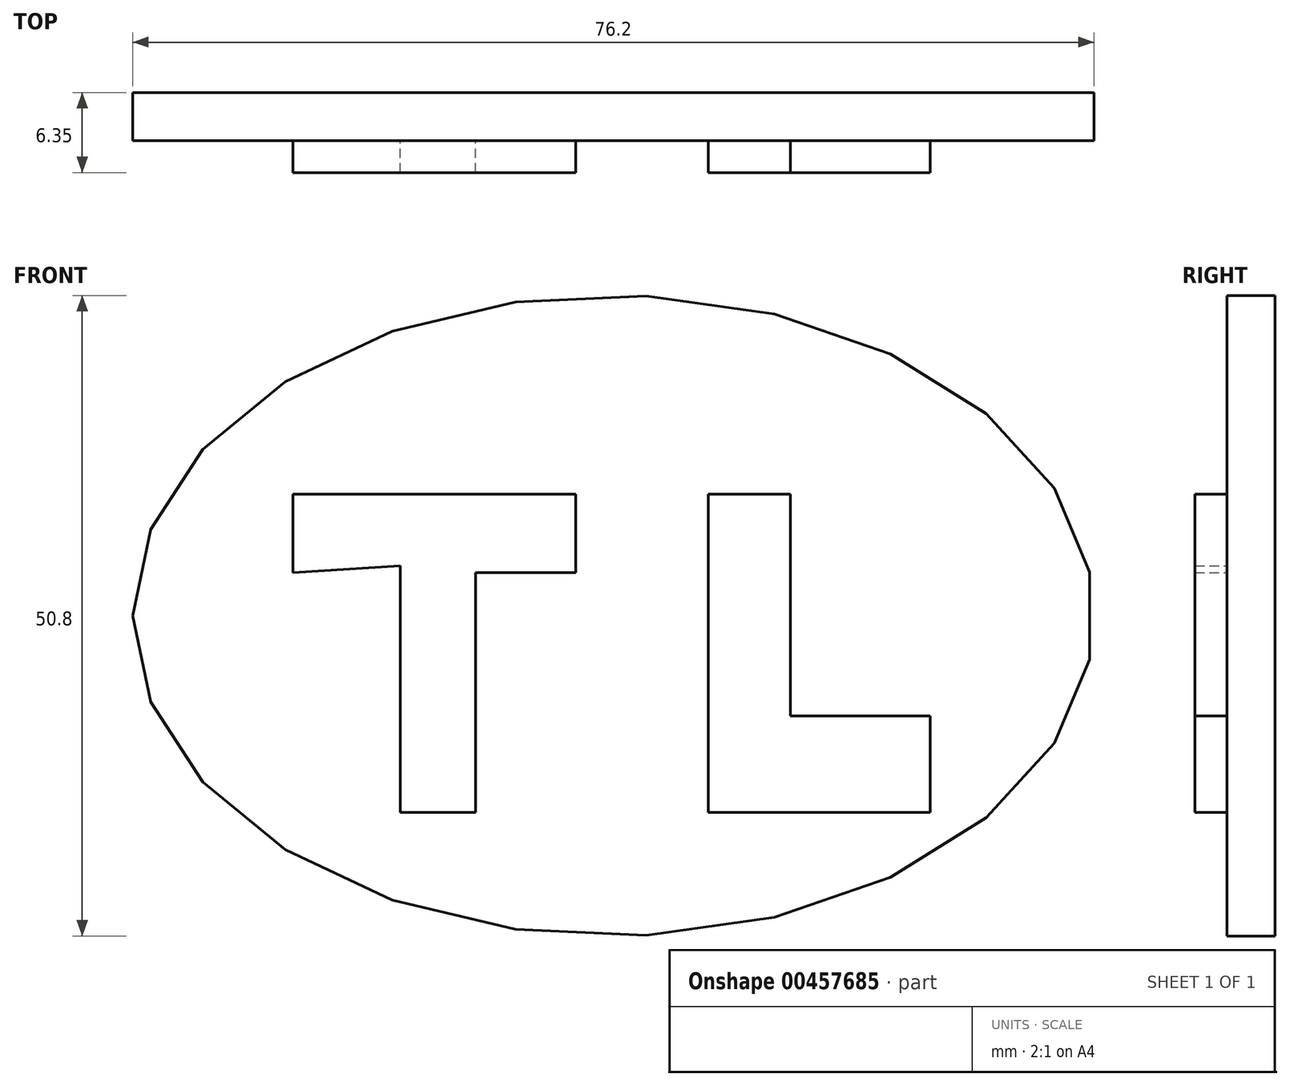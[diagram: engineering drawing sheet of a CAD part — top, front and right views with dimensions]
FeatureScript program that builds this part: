
annotation { "Feature Type Name" : "Feature", "Feature Type Description" : "" }
export const myFeature = defineFeature(function(context is Context, id is Id, definition is map)
    precondition{}
    {
        {
            var Q0;
            Q0=qCreatedBy(makeId("Front.planeOp"),FACE);
            var sketch = newSketch(context, id + "F0", { "sketchPlane" : qUnion([Q0])});
            skEllipse(sketch, "E0", {"center": v(0, 0) * mm, "majorRadius": 38.1 * mm, "minorRadius": 25.4 * mm, "majorAxis": v(-1, 0)});
            skSolve(sketch);
        }
        {
            var Q0;
            Q0 = qSketchRegion(id + "F0", true);
            extrude(context, id + "F1", {"entities" : qUnion([Q0]), "depth" : 3.8 * mm});
        }
        {
            var Q0;
            Q0=qCreatedBy(makeId("Front.planeOp"),FACE);
            var sketch = newSketch(context, id + "F2", { "sketchPlane" : qUnion([Q0])});
            skLineSegment(sketch, "E1", {"start": v(-16.88, 3.97) * mm, "end": v(-16.88, -15.6) * mm});
            skLineSegment(sketch, "E2", {"start": v(-16.88, -15.6) * mm, "end": v(-10.92, -15.6) * mm});
            skLineSegment(sketch, "E3", {"start": v(-10.92, -15.6) * mm, "end": v(-10.92, 3.4) * mm});
            skLineSegment(sketch, "E4", {"start": v(-10.92, 3.4) * mm, "end": v(-2.98, 3.4) * mm});
            skLineSegment(sketch, "E5", {"start": v(-2.98, 3.4) * mm, "end": v(-2.98, 9.65) * mm});
            skLineSegment(sketch, "E6", {"start": v(-2.98, 9.65) * mm, "end": v(-25.4, 9.65) * mm});
            skLineSegment(sketch, "E7", {"start": v(-25.4, 9.65) * mm, "end": v(-25.4, 3.4) * mm});
            skLineSegment(sketch, "E8", {"start": v(-25.4, 3.4) * mm, "end": v(-16.88, 3.97) * mm});
            skLineSegment(sketch, "E9", {"start": v(7.52, 9.65) * mm, "end": v(7.52, -15.6) * mm});
            skLineSegment(sketch, "E10", {"start": v(7.52, -15.6) * mm, "end": v(25.1, -15.6) * mm});
            skLineSegment(sketch, "E11", {"start": v(25.1, -15.6) * mm, "end": v(25.1, -7.94) * mm});
            skLineSegment(sketch, "E12", {"start": v(25.1, -7.94) * mm, "end": v(14.04, -7.94) * mm});
            skLineSegment(sketch, "E13", {"start": v(14.04, -7.94) * mm, "end": v(14.04, 9.65) * mm});
            skLineSegment(sketch, "E14", {"start": v(14.04, 9.65) * mm, "end": v(7.52, 9.65) * mm});
            skSolve(sketch);
        }
        {
            var Q0;
            Q0 = qSketchRegion(id + "F2", true);
            extrude(context, id + "F3", {"entities" : qUnion([Q0]), "operationType" : NewBodyOperationType.ADD, "depth" : 6.35 * mm});
        }
    });
